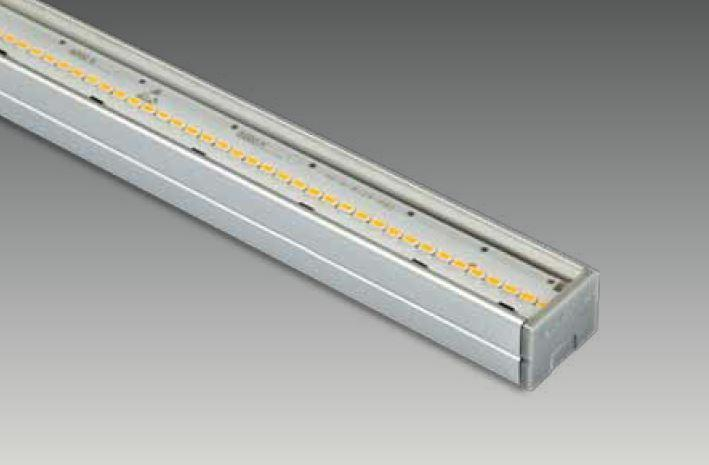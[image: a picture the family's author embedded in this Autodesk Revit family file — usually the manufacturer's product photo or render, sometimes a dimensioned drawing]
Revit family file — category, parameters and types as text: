
# Revit family: SD 0250 LIG
name_source: partatom
category: Lighting Fixtures
revit_build: Autodesk Revit 2017 (Build: 20160225_1515(x64)
units: mm (PartAtom-declared; Revit-internal decimal feet)

## family parameters
Cut with Voids When Loaded = No
Host = Face
Light Source = Yes
Part Type = Normal
Room Calculation Point = No
Round Connector Dimension = Use Diameter
Shared = No

## types (1)
- SDLIG.250.5.30.110
    Color Filter = 16777215
    Default Elevation = 1219 mm
    Dimming Lamp Color Temperature Shift = <None>
    Emit Shape Visible in Rendering = Yes
    Emit from Rectangle Length = 15 mm  [stored 0.0492126 ft]
    Emit from Rectangle Width = 250 mm  [stored 0.82021 ft]
    Light Source Symbol Size = 610 mm
    Manufacturer = ARLIGHT
    Type Image = SD 0250 LIG.JPG
    Wattage Comments = 5

note: [stored X ft] marks values corroborated as IEEE doubles in the binary element streams (Revit-internal decimal feet)

## geometry (parser evidence)
native form markers: Sweep x2
no freeform markers — native parametric forms only
